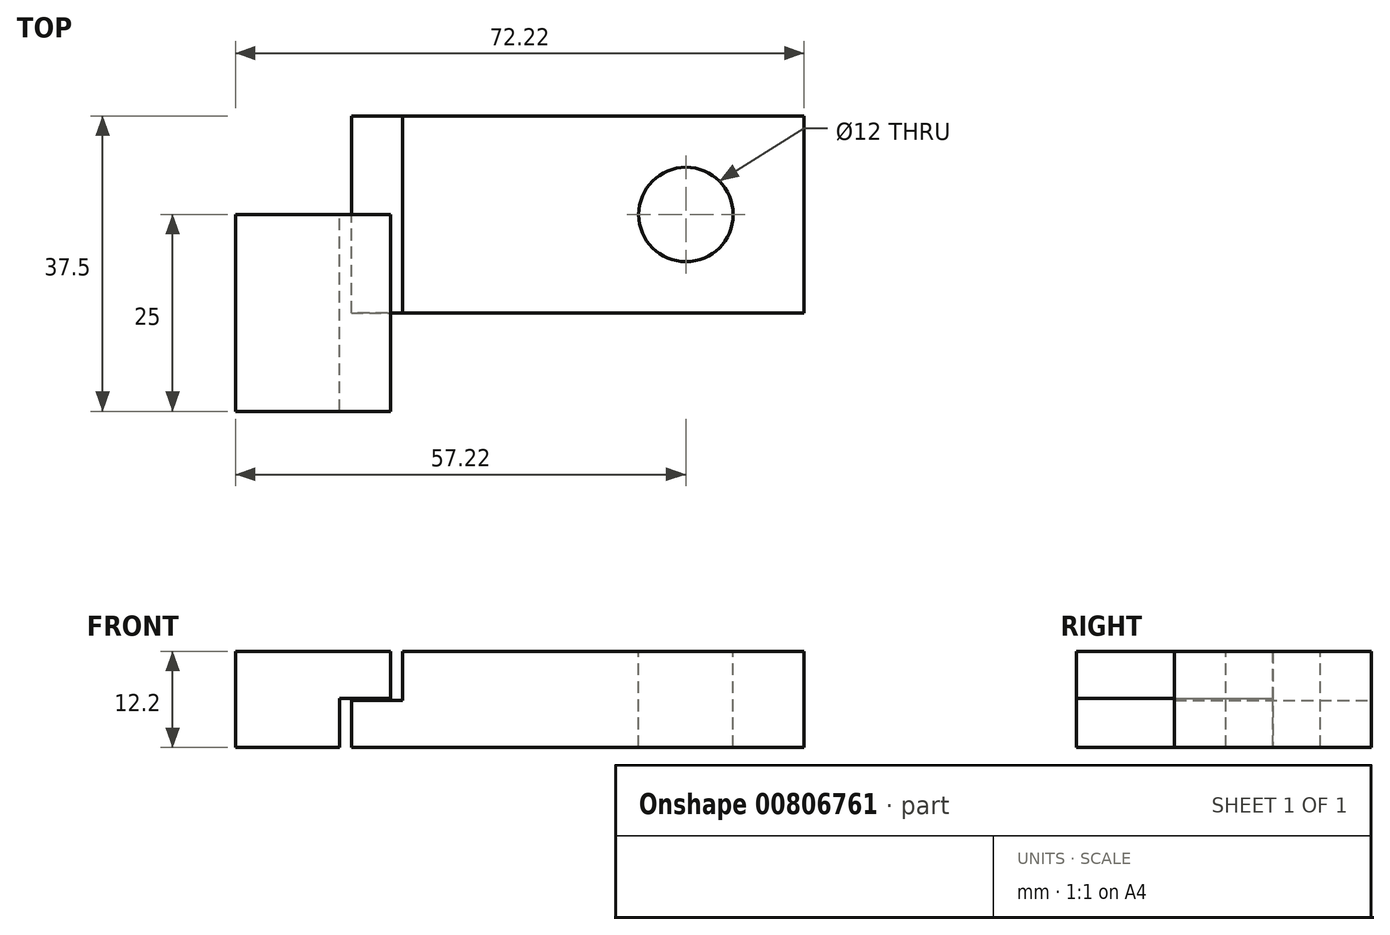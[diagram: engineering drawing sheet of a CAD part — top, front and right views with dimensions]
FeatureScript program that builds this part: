
annotation { "Feature Type Name" : "Feature", "Feature Type Description" : "" }
export const myFeature = defineFeature(function(context is Context, id is Id, definition is map)
    precondition{}
    {
        {
            var Q0;
            Q0=qCreatedBy(makeId("Front.planeOp"),FACE);
            var sketch = newSketch(context, id + "F0", { "sketchPlane" : qUnion([Q0])});
            skLineSegment(sketch, "E0", {"start": v(0, 0) * mm, "end": v(57.7, 0) * mm, "construction": true});
            skLineSegment(sketch, "E1", {"start": v(0, -0.1) * mm, "end": v(6.5, -0.1) * mm});
            skLineSegment(sketch, "E2", {"start": v(6.5, -0.1) * mm, "end": v(6.5, 6.1) * mm});
            skLineSegment(sketch, "E3", {"start": v(6.5, 6.1) * mm, "end": v(57.5, 6.1) * mm});
            skLineSegment(sketch, "E4", {"start": v(57.5, 6.1) * mm, "end": v(57.5, -6.1) * mm});
            skLineSegment(sketch, "E5", {"start": v(57.5, -6.1) * mm, "end": v(0, -6.1) * mm});
            skLineSegment(sketch, "E6", {"start": v(0, -6.1) * mm, "end": v(0, -0.1) * mm});
            skSolve(sketch);
        }
        {
            var Q0;
            Q0=qSketchRegion(id+"F0",true);
            extrude(context, id + "F1", {"entities" : qUnion([Q0]), "endBound" : BoundingType.SYMMETRIC, "depth" : 25 * mm, "offsetDistance" : 25 * mm});
        }
        {
            var Q0;
            Q0=makeQuery(id+"F1.opExtrude","SWEPT_FACE",FACE,{"disambiguationData":[OSD([sQuery(id+"F0.wireOp",EDGE,"E3")])]});
            var sketch = newSketch(context, id + "F2", { "sketchPlane" : qUnion([Q0])});
            skCircle(sketch, "E7", {"center": v(42.5, 0) * mm, "radius": 6 * mm});
            skSolve(sketch);
        }
        {
            var Q0;
            Q0=qSketchRegion(id+"F2",true);
            extrude(context, id + "F3", {"entities" : qUnion([Q0]), "operationType" : NewBodyOperationType.REMOVE, "endBound" : BoundingType.THROUGH_ALL, "oppositeDirection" : true, "depth" : 25 * mm, "offsetDistance" : 25 * mm});
        }
        {
            var Q0;
            Q0=qCreatedBy(makeId("Front.planeOp"),FACE);
            var sketch = newSketch(context, id + "F4", { "sketchPlane" : qUnion([Q0])});
            skLineSegment(sketch, "E8", {"start": v(5, 0.1) * mm, "end": v(5, 6.1) * mm});
            skLineSegment(sketch, "E9", {"start": v(5, 6.1) * mm, "end": v(-14.72, 6.1) * mm});
            skLineSegment(sketch, "E10", {"start": v(-14.72, 6.1) * mm, "end": v(-14.72, -6.1) * mm});
            skLineSegment(sketch, "E11", {"start": v(-14.72, -6.1) * mm, "end": v(-1.5, -6.1) * mm});
            skLineSegment(sketch, "E12", {"start": v(-1.5, -6.1) * mm, "end": v(-1.5, 0.1) * mm});
            skLineSegment(sketch, "E13", {"start": v(-1.5, 0.1) * mm, "end": v(5, 0.1) * mm});
            skLineSegment(sketch, "E14", {"start": v(-9.47, 0) * mm, "end": v(-1.2, 0) * mm, "construction": true});
            skSolve(sketch);
        }
        {
            var Q0;
            Q0 = qSketchRegion(id + "F4", true);
            extrude(context, id + "F5", {"entities" : qUnion([Q0]), "depth" : 25 * mm, "offsetDistance" : 25 * mm});
        }
    });
